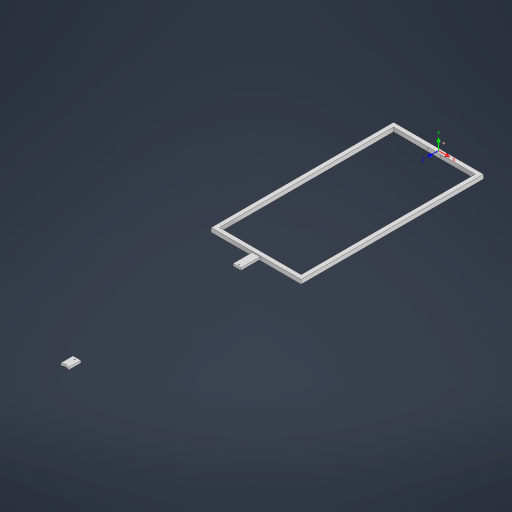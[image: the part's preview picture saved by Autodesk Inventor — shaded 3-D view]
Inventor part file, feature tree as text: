
AUTODESK INVENTOR PART (.ipt)
format: ipt  version: 2024 (Build 280153000, 153)  size: 253,440 bytes
history: native  units: mm
features: other x13, sketch x6, extrude x5, plane x1
ambient origin geometry x8: Origin, YZ Plane, XZ Plane, XY Plane, X Axis, Y Axis, Z Axis, Center Point
bodies: Body1 (feature_tree)
feature tree (25):
  other  "Sólido1"
  sketch  "Boceto2"  dims[d16=105.8mm d17=81.0mm]
  extrude  "Extrusión1"  Depth=81.0mm
  extrude  "Extrusión2"  Depth=28.4mm
  extrude  "Extrusión3"  Depth=150.0mm
  extrude  "Extrusión4"  TaperAngle=0.0deg  [1 undecoded]
  plane  "Plano de trabajo1"
  sketch  "Boceto5"  dims[d23=150.0mm d24=0.0mm]
  other  "Punto de trabajo1"
  other  "Punto de trabajo2"
  other  "Punto de trabajo3"
  other  "Punto de trabajo4"
  sketch  "Boceto6"  dims[d25=15.0mm d26=0.0mm d27=8.0mm d28=0.0mm]
  other  "SCU1"
  extrude  "Extrusión5"  Depth=8.0mm TaperAngle=0.0deg
  sketch  "Boceto3"  dims[d18=700.0mm d19=28.4mm]
  sketch  "Boceto4"  dims[d21=666.0mm d22=150.0mm]
  sketch  "Boceto7"  dims[d29=15.0mm d30=15.0mm d31=15.0mm d32=15.0mm d33=15.0mm d34=0.0mm d35=70.0mm d36=45.0mm d37=4.0mm d38=4.0mm d39=15.0mm d40=0.0mm d41=164.2mm d42=7.5mm d43=0.0mm d44=0.0mm d45=0.0mm d46=0.0mm d47=0.0mm d48=0.0mm d49=666.0mm d50=4.0mm d51=4.0mm d52=124.2mm d53=174.2mm d54=50.0mm d55=7.5mm d56=10.0mm d57=0.0mm]
  other  "SCU1: Plano YZ"
  other  "SCU1: Plano XZ"
  other  "SCU1: Plano XY"
  other  "SCU1: Eje X"
  other  "SCU1: Eje Y"
  other  "SCU1: Eje Z"
  other  "SCU1: Centro"
note: 1 required parameter value undecoded (feature->parameter linkage not recoverable at this tier; creation-order binding heuristic only, values carry confidence <= 0.55)
